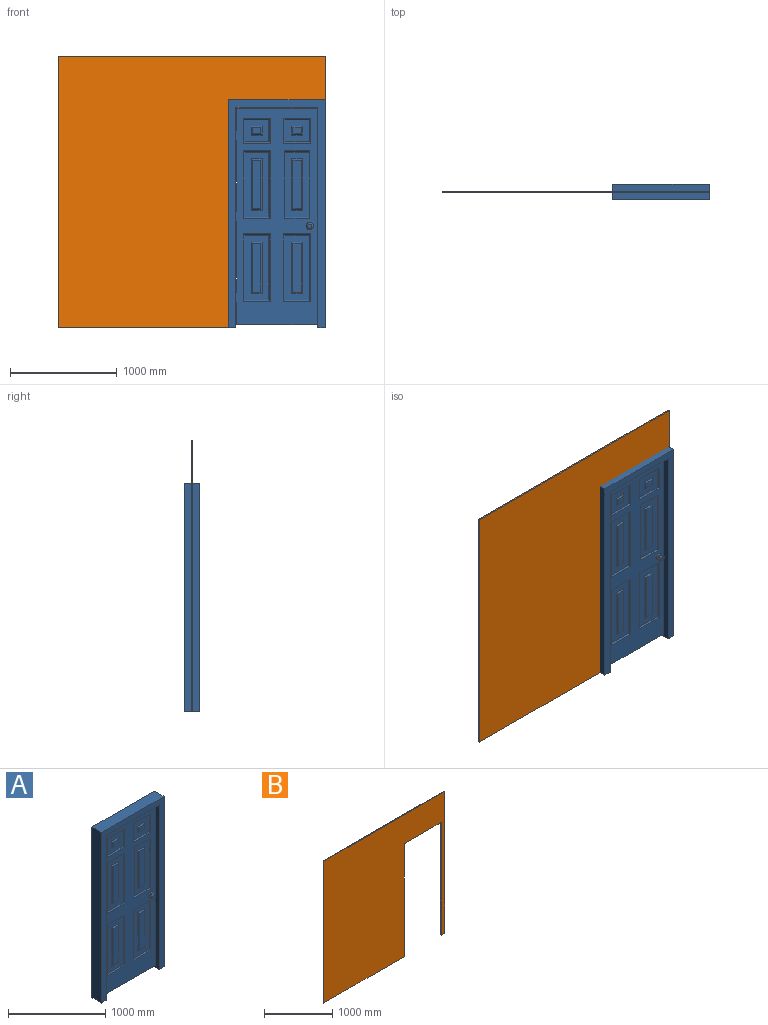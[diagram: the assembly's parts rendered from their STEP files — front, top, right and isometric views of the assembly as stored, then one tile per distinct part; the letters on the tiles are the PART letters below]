
ASSEMBLY  parts=2 mates=1
PART A: 157 faces, bbox 908.1x139.7x2140 mm
  f0: plane 2032x762mm, normal (0,1,0), area 768948.7mm2, adj f2,f12,f13,f14,f15,f16,f17,f18
  f1: plane 2032x762mm, normal (0,-1,0), area 785077.7mm2, adj f2,f12,f13,f14,f15,f16,f17,f18
  f2: plane 2070.1x139.7mm, normal (1,0,0), area 279213.2mm2, adj f0,f1,f3,f9,f10,f11,f12,f13
  f3: plane 768.35x139.7mm, normal (0,0,-1), area 107338.5mm2, adj f2,f4,f10,f11
  f4: plane 2070.1x139.7mm, normal (-1,0,0), area 289193mm2, adj f3,f5,f10,f11
  f5: plane 139.7x69.85mm, normal (0,0,-1), area 9758mm2, adj f4,f6,f10,f11
  f6: plane 2139.95x139.7mm, normal (1,0,0), area 298951mm2, adj f5,f7,f10,f11
  f7: plane 908.05x139.7mm, normal (0,0,1), area 126854.6mm2, adj f6,f8,f10,f11
  f8: plane 2139.95x139.7mm, normal (-1,0,0), area 298951mm2, adj f7,f9,f10,f11
  f9: plane 139.7x69.85mm, normal (0,0,-1), area 9758mm2, adj f2,f8,f10,f11
  f10: plane 2139.95x908.05mm, normal (0,-1,0), area 352620.3mm2, adj f2,f3,f4,f5,f6,f7,f8,f9
  f11: plane 2139.95x908.05mm, normal (0,1,0), area 352620.3mm2, adj f2,f3,f4,f5,f6,f7,f8,f9
  f12: plane 34.93x6.35mm, normal (0,0,1), area 221.8mm2, adj f0,f1,f2,f24
  f13: plane 34.93x6.35mm, normal (0,0,-1), area 221.8mm2, adj f0,f1,f2,f14
  f14: plane 663.58x34.93mm, normal (-1,0,0), area 23175.4mm2, adj f0,f1,f13,f15
  f15: plane 34.93x6.35mm, normal (0,0,1), area 221.8mm2, adj f0,f1,f2,f14
  f16: plane 34.93x6.35mm, normal (0,0,-1), area 221.8mm2, adj f0,f1,f2,f17
  f17: plane 209.55x34.93mm, normal (-1,0,0), area 7318.5mm2, adj f0,f1,f16,f18
  f18: plane 755.65x34.93mm, normal (0,0,-1), area 26391.1mm2, adj f0,f1,f17,f19
  f19: plane 2032x34.93mm, normal (1,0,0), area 70967.6mm2, adj f0,f1,f18,f20
  f20: plane 755.65x34.93mm, normal (0,0,1), area 26391.1mm2, adj f0,f1,f19,f21
  f21: plane 209.55x34.93mm, normal (-1,0,0), area 7318.5mm2, adj f0,f1,f20,f22
  f22: plane 34.93x6.35mm, normal (0,0,1), area 221.8mm2, adj f0,f1,f2,f21
  f23: plane 34.93x6.35mm, normal (0,0,-1), area 221.8mm2, adj f0,f1,f2,f24
  f24: plane 663.58x34.93mm, normal (-1,0,0), area 23175.4mm2, adj f0,f1,f12,f23
  f25: plane 228.6x209.55mm, normal (0,-1,0), area 39516.1mm2, adj f57,f58,f59,f60,f77,f78,f79,f80
  f26: plane 76.2x57.15mm, normal (0,-1,0), area 4354.8mm2, adj f77,f78,f79,f80
  f27: plane 609.6x228.6mm, normal (0,-1,0), area 90322.4mm2, adj f39,f40,f41,f42,f61,f62,f63,f64
  f28: plane 609.6x228.6mm, normal (0,-1,0), area 90322.4mm2, adj f48,f49,f50,f51,f81,f82,f83,f84
  f29: plane 228.6x209.55mm, normal (0,-1,0), area 39516mm2, adj f53,f54,f55,f56,f73,f74,f75,f76
  f30: plane 635x12.7mm, normal (1,0,0), area 7903.2mm2, adj f1,f32,f47,f52
  f31: plane 635x12.7mm, normal (-1,0,0), area 7903.2mm2, adj f1,f32,f47,f52
  f32: plane 609.6x228.6mm, normal (0,-1,0), area 90322.4mm2, adj f30,f31,f47,f52,f69,f70,f71,f72
  f33: plane 457.2x76.2mm, normal (0,-1,0), area 34838.6mm2, adj f69,f70,f71,f72
  f34: plane 609.6x228.6mm, normal (0,-1,0), area 90322.4mm2, adj f43,f44,f45,f46,f65,f66,f67,f68
  f35: plane 457.2x76.2mm, normal (0,-1,0), area 34838.6mm2, adj f65,f66,f67,f68
  f36: plane 457.2x76.2mm, normal (0,-1,0), area 34838.6mm2, adj f61,f62,f63,f64
  f37: plane 457.2x76.2mm, normal (0,-1,0), area 34838.6mm2, adj f81,f82,f83,f84
  f38: plane 76.2x57.15mm, normal (0,-1,0), area 4354.8mm2, adj f73,f74,f75,f76
  f39: plane 254x12.7mm, normal (0,-0.71,-0.71), area 4333.9mm2, adj f1,f27,f40,f41
  f40: plane 635x12.7mm, normal (-0.71,-0.71,0), area 11176.8mm2, adj f1,f27,f39,f42
  f41: plane 635x12.7mm, normal (0.71,-0.71,0), area 11176.8mm2, adj f1,f27,f39,f42
  f42: plane 254x12.7mm, normal (0,-0.71,0.71), area 4333.9mm2, adj f1,f27,f40,f41
  f43: plane 254x12.7mm, normal (0,-0.71,-0.71), area 4333.9mm2, adj f1,f34,f44,f45
  f44: plane 635x12.7mm, normal (0.71,-0.71,0), area 11176.8mm2, adj f1,f34,f43,f46
  f45: plane 635x12.7mm, normal (-0.71,-0.71,0), area 11176.8mm2, adj f1,f34,f43,f46
  f46: plane 254x12.7mm, normal (0,-0.71,0.71), area 4333.9mm2, adj f1,f34,f44,f45
  f47: plane 228.6x12.7mm, normal (0,-0.71,0.71), area 4105.8mm2, adj f1,f30,f31,f32
  f48: plane 254x12.7mm, normal (0,-0.71,-0.71), area 4333.9mm2, adj f1,f28,f49,f50
  f49: plane 635x12.7mm, normal (-0.71,-0.71,0), area 11176.8mm2, adj f1,f28,f48,f51
  f50: plane 635x12.7mm, normal (0.71,-0.71,0), area 11176.8mm2, adj f1,f28,f48,f51
  f51: plane 254x12.7mm, normal (0,-0.71,0.71), area 4333.9mm2, adj f1,f28,f49,f50
  f52: plane 228.6x12.7mm, normal (0,-0.71,-0.71), area 4105.8mm2, adj f1,f30,f31,f32
  f53: plane 254x12.7mm, normal (0,-0.71,-0.71), area 4333.9mm2, adj f1,f29,f54,f55
  f54: plane 234.95x12.7mm, normal (-0.71,-0.71,0), area 3991.7mm2, adj f1,f29,f53,f56
  f55: plane 234.95x12.7mm, normal (0.71,-0.71,0), area 3991.7mm2, adj f1,f29,f53,f56
  f56: plane 254x12.7mm, normal (0,-0.71,0.71), area 4333.9mm2, adj f1,f29,f54,f55
  f57: plane 254x12.7mm, normal (0,-0.71,-0.71), area 4333.9mm2, adj f1,f25,f58,f59
  f58: plane 234.95x12.7mm, normal (0.71,-0.71,0), area 3991.7mm2, adj f1,f25,f57,f60
  f59: plane 234.95x12.7mm, normal (-0.71,-0.71,0), area 3991.7mm2, adj f1,f25,f57,f60
  f60: plane 254x12.7mm, normal (0,-0.71,0.71), area 4333.9mm2, adj f1,f25,f58,f59
  f61: plane 482.6x12.7mm, normal (-0.71,-0.71,0), area 8439.6mm2, adj f27,f36,f62,f63
  f62: plane 101.6x12.7mm, normal (0,-0.71,0.71), area 1596.7mm2, adj f27,f36,f61,f64
  f63: plane 101.6x12.7mm, normal (0,-0.71,-0.71), area 1596.7mm2, adj f27,f36,f61,f64
  f64: plane 482.6x12.7mm, normal (0.71,-0.71,0), area 8439.6mm2, adj f27,f36,f62,f63
  f65: plane 101.6x12.7mm, normal (0,-0.71,0.71), area 1596.7mm2, adj f34,f35,f66,f67
  f66: plane 482.6x12.7mm, normal (-0.71,-0.71,0), area 8439.6mm2, adj f34,f35,f65,f68
  f67: plane 482.6x12.7mm, normal (0.71,-0.71,0), area 8439.6mm2, adj f34,f35,f65,f68
  f68: plane 101.6x12.7mm, normal (0,-0.71,-0.71), area 1596.7mm2, adj f34,f35,f66,f67
  f69: plane 482.6x12.7mm, normal (0.71,-0.71,0), area 8439.6mm2, adj f32,f33,f70,f71
  f70: plane 101.6x12.7mm, normal (0,-0.71,0.71), area 1596.7mm2, adj f32,f33,f69,f72
  f71: plane 101.6x12.7mm, normal (0,-0.71,-0.71), area 1596.7mm2, adj f32,f33,f69,f72
  f72: plane 482.6x12.7mm, normal (-0.71,-0.71,0), area 8439.6mm2, adj f32,f33,f70,f71
  f73: plane 101.6x12.7mm, normal (0,-0.71,0.71), area 1596.7mm2, adj f29,f38,f74,f75
  f74: plane 82.55x12.7mm, normal (0.71,-0.71,0), area 1254.5mm2, adj f29,f38,f73,f76
  f75: plane 82.55x12.7mm, normal (-0.71,-0.71,0), area 1254.5mm2, adj f29,f38,f73,f76
  f76: plane 101.6x12.7mm, normal (0,-0.71,-0.71), area 1596.7mm2, adj f29,f38,f74,f75
  f77: plane 101.6x12.7mm, normal (0,-0.71,0.71), area 1596.7mm2, adj f25,f26,f78,f79
  f78: plane 82.55x12.7mm, normal (-0.71,-0.71,0), area 1254.5mm2, adj f25,f26,f77,f80
  f79: plane 82.55x12.7mm, normal (0.71,-0.71,0), area 1254.5mm2, adj f25,f26,f77,f80
  f80: plane 101.6x12.7mm, normal (0,-0.71,-0.71), area 1596.7mm2, adj f25,f26,f78,f79
  f81: plane 101.6x12.7mm, normal (0,-0.71,0.71), area 1596.7mm2, adj f28,f37,f82,f83
  f82: plane 482.6x12.7mm, normal (0.71,-0.71,0), area 8439.6mm2, adj f28,f37,f81,f84
  f83: plane 482.6x12.7mm, normal (-0.71,-0.71,0), area 8439.6mm2, adj f28,f37,f81,f84
  f84: plane 101.6x12.7mm, normal (0,-0.71,-0.71), area 1596.7mm2, adj f28,f37,f82,f83
  f85: plane 228.6x209.55mm, normal (0,1,0), area 39516mm2, adj f117,f118,f119,f120,f141,f142,f143,f144
  f86: plane 76.2x57.15mm, normal (0,1,0), area 4354.8mm2, adj f141,f142,f143,f144
  f87: plane 609.6x228.6mm, normal (0,1,0), area 90322.4mm2, adj f97,f98,f99,f100,f125,f126,f127,f128
  f88: plane 457.2x76.2mm, normal (0,1,0), area 34838.6mm2, adj f125,f126,f127,f128
  f89: plane 228.6x209.55mm, normal (0,1,0), area 39516.1mm2, adj f113,f114,f115,f116,f137,f138,f139,f140
  f90: plane 609.6x228.6mm, normal (0,1,0), area 90322.4mm2, adj f105,f106,f107,f108,f133,f134,f135,f136
  f91: plane 609.6x228.6mm, normal (0,1,0), area 90322.4mm2, adj f109,f110,f111,f112,f129,f130,f131,f132
  f92: plane 457.2x76.2mm, normal (0,1,0), area 34838.6mm2, adj f129,f130,f131,f132
  f93: plane 609.6x228.6mm, normal (0,1,0), area 90322.4mm2, adj f101,f102,f103,f104,f121,f122,f123,f124
  f94: plane 76.2x57.15mm, normal (0,1,0), area 4354.8mm2, adj f137,f138,f139,f140
  f95: plane 457.2x76.2mm, normal (0,1,0), area 34838.6mm2, adj f133,f134,f135,f136
  f96: plane 457.2x76.2mm, normal (0,1,0), area 34838.6mm2, adj f121,f122,f123,f124
  f97: plane 254x12.7mm, normal (0,0.71,-0.71), area 4333.9mm2, adj f0,f87,f98,f99
  f98: plane 635x12.7mm, normal (-0.71,0.71,0), area 11176.8mm2, adj f0,f87,f97,f100
  f99: plane 635x12.7mm, normal (0.71,0.71,0), area 11176.8mm2, adj f0,f87,f97,f100
  f100: plane 254x12.7mm, normal (0,0.71,0.71), area 4333.9mm2, adj f0,f87,f98,f99
  f101: plane 254x12.7mm, normal (0,0.71,-0.71), area 4333.9mm2, adj f0,f93,f102,f103
  f102: plane 635x12.7mm, normal (0.71,0.71,0), area 11176.8mm2, adj f0,f93,f101,f104
  f103: plane 635x12.7mm, normal (-0.71,0.71,0), area 11176.8mm2, adj f0,f93,f101,f104
  f104: plane 254x12.7mm, normal (0,0.71,0.71), area 4333.9mm2, adj f0,f93,f102,f103
  f105: plane 254x12.7mm, normal (0,0.71,-0.71), area 4333.9mm2, adj f0,f90,f106,f107
  f106: plane 635x12.7mm, normal (0.71,0.71,0), area 11176.8mm2, adj f0,f90,f105,f108
  f107: plane 635x12.7mm, normal (-0.71,0.71,0), area 11176.8mm2, adj f0,f90,f105,f108
  f108: plane 254x12.7mm, normal (0,0.71,0.71), area 4333.9mm2, adj f0,f90,f106,f107
  f109: plane 254x12.7mm, normal (0,0.71,-0.71), area 4333.9mm2, adj f0,f91,f110,f111
  f110: plane 635x12.7mm, normal (-0.71,0.71,0), area 11176.8mm2, adj f0,f91,f109,f112
  f111: plane 635x12.7mm, normal (0.71,0.71,0), area 11176.8mm2, adj f0,f91,f109,f112
  f112: plane 254x12.7mm, normal (0,0.71,0.71), area 4333.9mm2, adj f0,f91,f110,f111
  f113: plane 254x12.7mm, normal (0,0.71,-0.71), area 4333.9mm2, adj f0,f89,f114,f115
  f114: plane 234.95x12.7mm, normal (0.71,0.71,0), area 3991.7mm2, adj f0,f89,f113,f116
  f115: plane 234.95x12.7mm, normal (-0.71,0.71,0), area 3991.7mm2, adj f0,f89,f113,f116
  f116: plane 254x12.7mm, normal (0,0.71,0.71), area 4333.9mm2, adj f0,f89,f114,f115
  f117: plane 234.95x12.7mm, normal (-0.71,0.71,0), area 3991.7mm2, adj f0,f85,f118,f119
  f118: plane 254x12.7mm, normal (0,0.71,-0.71), area 4333.9mm2, adj f0,f85,f117,f120
  f119: plane 254x12.7mm, normal (0,0.71,0.71), area 4333.9mm2, adj f0,f85,f117,f120
  f120: plane 234.95x12.7mm, normal (0.71,0.71,0), area 3991.7mm2, adj f0,f85,f118,f119
  f121: plane 482.6x12.7mm, normal (0.71,0.71,0), area 8439.6mm2, adj f93,f96,f122,f123
  f122: plane 101.6x12.7mm, normal (0,0.71,0.71), area 1596.7mm2, adj f93,f96,f121,f124
  f123: plane 101.6x12.7mm, normal (0,0.71,-0.71), area 1596.7mm2, adj f93,f96,f121,f124
  f124: plane 482.6x12.7mm, normal (-0.71,0.71,0), area 8439.6mm2, adj f93,f96,f122,f123
  f125: plane 101.6x12.7mm, normal (0,0.71,0.71), area 1596.7mm2, adj f87,f88,f126,f127
  f126: plane 482.6x12.7mm, normal (0.71,0.71,0), area 8439.6mm2, adj f87,f88,f125,f128
  f127: plane 482.6x12.7mm, normal (-0.71,0.71,0), area 8439.6mm2, adj f87,f88,f125,f128
  f128: plane 101.6x12.7mm, normal (0,0.71,-0.71), area 1596.7mm2, adj f87,f88,f126,f127
  f129: plane 482.6x12.7mm, normal (-0.71,0.71,0), area 8439.6mm2, adj f91,f92,f130,f131
  f130: plane 101.6x12.7mm, normal (0,0.71,0.71), area 1596.7mm2, adj f91,f92,f129,f132
  f131: plane 101.6x12.7mm, normal (0,0.71,-0.71), area 1596.7mm2, adj f91,f92,f129,f132
  f132: plane 482.6x12.7mm, normal (0.71,0.71,0), area 8439.6mm2, adj f91,f92,f130,f131
  f133: plane 101.6x12.7mm, normal (0,0.71,0.71), area 1596.7mm2, adj f90,f95,f134,f135
  f134: plane 482.6x12.7mm, normal (-0.71,0.71,0), area 8439.6mm2, adj f90,f95,f133,f136
  f135: plane 482.6x12.7mm, normal (0.71,0.71,0), area 8439.6mm2, adj f90,f95,f133,f136
  f136: plane 101.6x12.7mm, normal (0,0.71,-0.71), area 1596.7mm2, adj f90,f95,f134,f135
  f137: plane 101.6x12.7mm, normal (0,0.71,0.71), area 1596.7mm2, adj f89,f94,f138,f139
  f138: plane 82.55x12.7mm, normal (-0.71,0.71,0), area 1254.5mm2, adj f89,f94,f137,f140
  f139: plane 82.55x12.7mm, normal (0.71,0.71,0), area 1254.5mm2, adj f89,f94,f137,f140
  f140: plane 101.6x12.7mm, normal (0,0.71,-0.71), area 1596.7mm2, adj f89,f94,f138,f139
  f141: plane 101.6x12.7mm, normal (0,0.71,0.71), area 1596.7mm2, adj f85,f86,f142,f143
  f142: plane 82.55x12.7mm, normal (0.71,0.71,0), area 1254.5mm2, adj f85,f86,f141,f144
  f143: plane 82.55x12.7mm, normal (-0.71,0.71,0), area 1254.5mm2, adj f85,f86,f141,f144
  f144: plane 101.6x12.7mm, normal (0,0.71,-0.71), area 1596.7mm2, adj f85,f86,f142,f143
  f145: plane 44.45x44.45mm, normal (0,-1,0), area 1266.8mm2, adj f146,f147
  f146: cone r=22.23mm half-angle=45deg, axis (0,1,0), area 3224.7mm2, adj f1,f145
  f147: cylinder r=9.53mm len=19.05mm, axis (0,1,0), area 760.1mm2, adj f145,f149
  f148: plane 38.1x38.1mm, normal (0,-1,0), area 1140.1mm2, adj f150
  f149: plane 38.1x38.1mm, normal (0,1,0), area 855.1mm2, adj f147,f150
  f150: torus R=19.05mm, axis (0,-1,0), area 6802.4mm2, adj f148,f149
  f151: plane 44.45x44.45mm, normal (0,1,0), area 1266.8mm2, adj f152,f153
  f152: cone r=22.23mm half-angle=45deg, axis (0,-1,0), area 3224.7mm2, adj f0,f151
  f153: cylinder r=9.53mm len=19.05mm, axis (0,-1,0), area 760.1mm2, adj f151,f155
  f154: plane 38.1x38.1mm, normal (0,1,0), area 1140.1mm2, adj f156
  f155: plane 38.1x38.1mm, normal (0,-1,0), area 855.1mm2, adj f153,f156
  f156: torus R=19.05mm, axis (0,1,0), area 6802.4mm2, adj f154,f155
PART B: 10 faces, bbox 2514.6x12.7x2552.7 mm
  f0: plane 76.2x12.7mm, normal (0,0,-1), area 967.7mm2, adj f1,f2,f6,f8
  f1: plane 2552.7x2514.6mm, normal (0,-1,0), area 4857732.2mm2, adj f0,f3,f4,f5,f6,f7,f8,f9
  f2: plane 2552.7x2514.6mm, normal (0,1,0), area 4857732.2mm2, adj f0,f3,f4,f5,f6,f7,f8,f9
  f3: plane 2514.6x12.7mm, normal (0,0,1), area 31935.4mm2, adj f1,f2,f4,f6
  f4: plane 2552.7x12.7mm, normal (-1,0,0), area 32419.3mm2, adj f1,f2,f3,f5
  f5: plane 1670.05x12.7mm, normal (0,0,-1), area 21209.6mm2, adj f1,f2,f4,f7
  f6: plane 2552.7x12.7mm, normal (1,0,0), area 32419.3mm2, adj f0,f1,f2,f3
  f7: plane 2032x12.7mm, normal (1,0,0), area 25806.4mm2, adj f1,f2,f5,f9
  f8: plane 2032x12.7mm, normal (-1,0,0), area 25806.4mm2, adj f0,f1,f2,f9
  f9: plane 768.35x12.7mm, normal (0,0,-1), area 9758mm2, adj f1,f2,f7,f8
PLACE A t=(914.52,-7.25,-190.12)mm
PLACE B t=(117.59,-0.9,16.25)mm
MATE fastened B.f7 <-> A.f2  axis (1,0,0) through (530.34,-7.25,-1260.1)mm
